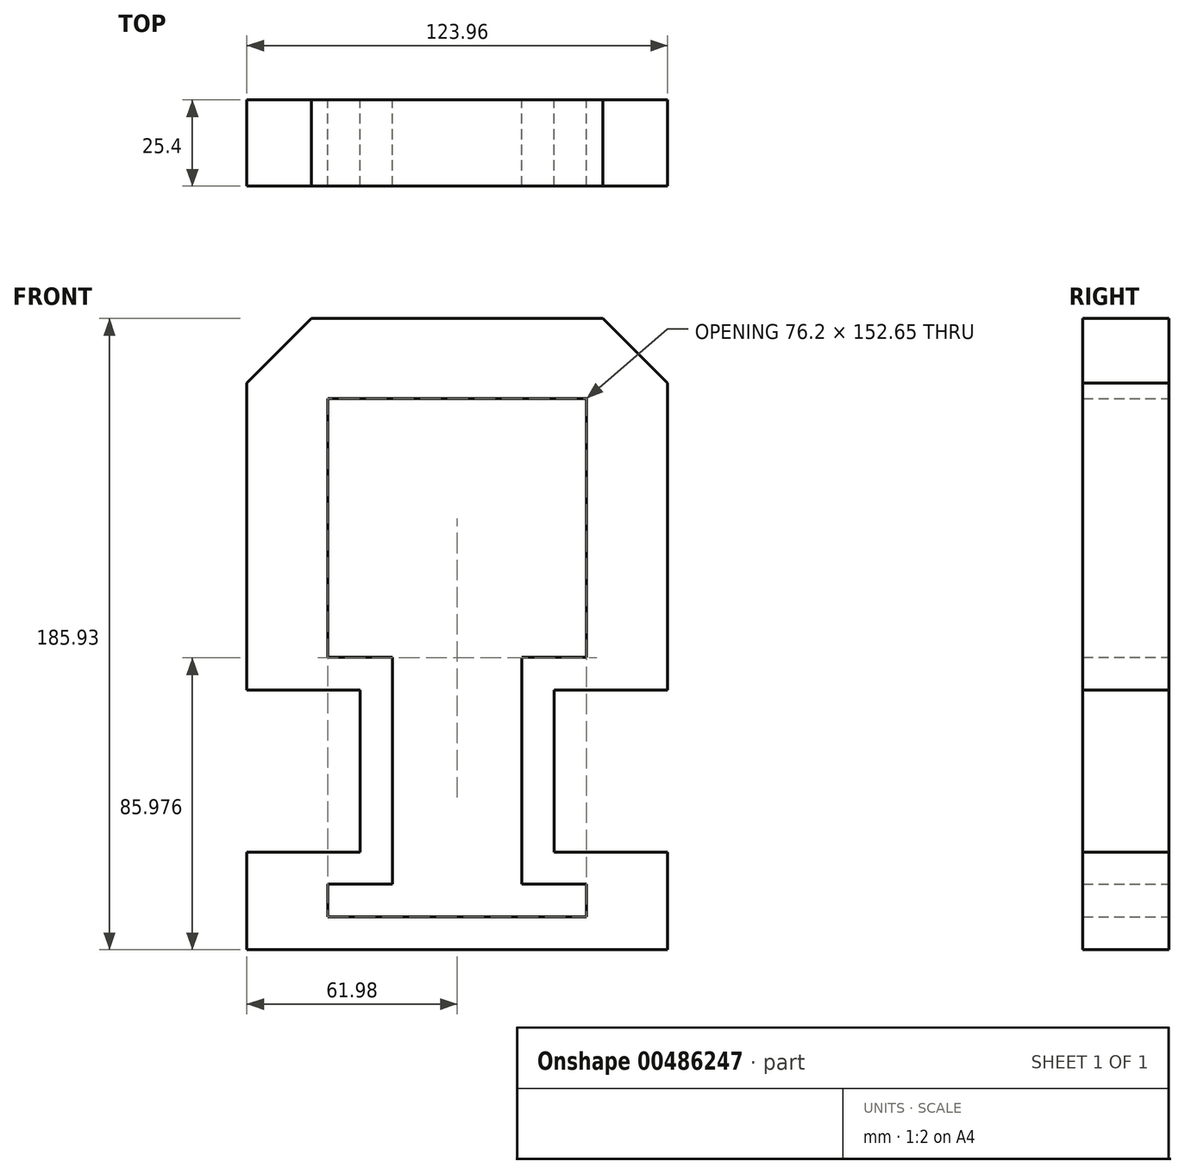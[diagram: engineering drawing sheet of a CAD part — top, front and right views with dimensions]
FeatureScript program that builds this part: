
annotation { "Feature Type Name" : "Feature", "Feature Type Description" : "" }
export const myFeature = defineFeature(function(context is Context, id is Id, definition is map)
    precondition{}
    {
        {
            var Q0;
            Q0=qCreatedBy(makeId("Front.planeOp"),FACE);
            var sketch = newSketch(context, id + "F0", { "sketchPlane" : qUnion([Q0])});
            skLineSegment(sketch, "E0", {"start": v(0, 54.64) * mm, "end": v(38.1, 54.64) * mm});
            skLineSegment(sketch, "E1", {"start": v(38.1, 54.64) * mm, "end": v(0, 54.64) * mm});
            skLineSegment(sketch, "E2", {"start": v(-38.1, 54.64) * mm, "end": v(0, 54.64) * mm});
            skLineSegment(sketch, "E3", {"start": v(-38.1, 54.64) * mm, "end": v(-38.1, -21.56) * mm});
            skLineSegment(sketch, "E4", {"start": v(-38.1, -21.56) * mm, "end": v(-38.1, 54.64) * mm});
            skLineSegment(sketch, "E5", {"start": v(38.1, 54.64) * mm, "end": v(38.1, -21.56) * mm});
            skLineSegment(sketch, "E6", {"start": v(38.1, -21.56) * mm, "end": v(38.1, 54.64) * mm});
            skLineSegment(sketch, "E7", {"start": v(-38.1, -21.56) * mm, "end": v(-19.05, -21.56) * mm});
            skLineSegment(sketch, "E8", {"start": v(-19.05, -21.56) * mm, "end": v(-38.1, -21.56) * mm});
            skLineSegment(sketch, "E9", {"start": v(38.1, -21.56) * mm, "end": v(19.05, -21.56) * mm});
            skLineSegment(sketch, "E10", {"start": v(19.05, -21.56) * mm, "end": v(38.1, -21.56) * mm});
            skLineSegment(sketch, "E11", {"start": v(-19.05, -21.56) * mm, "end": v(-19.05, -88.36) * mm});
            skLineSegment(sketch, "E12", {"start": v(-19.05, -88.36) * mm, "end": v(-19.05, -21.56) * mm});
            skLineSegment(sketch, "E13", {"start": v(19.05, -21.56) * mm, "end": v(19.05, -88.36) * mm});
            skLineSegment(sketch, "E14", {"start": v(19.05, -88.36) * mm, "end": v(19.05, -21.56) * mm});
            skLineSegment(sketch, "E15", {"start": v(19.05, -88.36) * mm, "end": v(38.1, -88.36) * mm});
            skLineSegment(sketch, "E16", {"start": v(38.1, -88.36) * mm, "end": v(19.05, -88.36) * mm});
            skLineSegment(sketch, "E17", {"start": v(-19.05, -88.36) * mm, "end": v(-38.1, -88.36) * mm});
            skLineSegment(sketch, "E18", {"start": v(-38.1, -88.36) * mm, "end": v(-19.05, -88.36) * mm});
            skLineSegment(sketch, "E19", {"start": v(-38.1, -88.36) * mm, "end": v(-38.1, -98.01) * mm});
            skLineSegment(sketch, "E20", {"start": v(-38.1, -98.01) * mm, "end": v(-38.1, -88.36) * mm});
            skLineSegment(sketch, "E21", {"start": v(-38.1, -98.01) * mm, "end": v(38.1, -98.01) * mm});
            skLineSegment(sketch, "E22", {"start": v(38.1, -98.01) * mm, "end": v(38.1, -88.36) * mm});
            skLineSegment(sketch, "E23", {"start": v(0, -107.66) * mm, "end": v(61.98, -107.66) * mm});
            skLineSegment(sketch, "E24", {"start": v(61.98, -107.66) * mm, "end": v(0, -107.66) * mm});
            skLineSegment(sketch, "E25", {"start": v(-61.98, -107.66) * mm, "end": v(0, -107.66) * mm});
            skLineSegment(sketch, "E26", {"start": v(61.98, -107.66) * mm, "end": v(61.98, -78.96) * mm});
            skLineSegment(sketch, "E27", {"start": v(61.98, -78.96) * mm, "end": v(61.98, -107.66) * mm});
            skLineSegment(sketch, "E28", {"start": v(-61.98, -107.66) * mm, "end": v(-61.98, -78.96) * mm});
            skLineSegment(sketch, "E29", {"start": v(-61.98, -78.96) * mm, "end": v(-28.57, -78.96) * mm});
            skLineSegment(sketch, "E30", {"start": v(-28.57, -78.96) * mm, "end": v(-61.98, -78.96) * mm});
            skLineSegment(sketch, "E31", {"start": v(61.98, -78.96) * mm, "end": v(28.58, -78.96) * mm});
            skLineSegment(sketch, "E32", {"start": v(28.58, -78.96) * mm, "end": v(61.98, -78.96) * mm});
            skLineSegment(sketch, "E33", {"start": v(-28.57, -78.96) * mm, "end": v(-28.57, -31.2) * mm});
            skLineSegment(sketch, "E34", {"start": v(28.58, -78.96) * mm, "end": v(28.58, -31.2) * mm});
            skLineSegment(sketch, "E35", {"start": v(28.58, -31.2) * mm, "end": v(61.98, -31.2) * mm});
            skLineSegment(sketch, "E36", {"start": v(61.98, -31.2) * mm, "end": v(28.58, -31.2) * mm});
            skLineSegment(sketch, "E37", {"start": v(-28.57, -31.2) * mm, "end": v(-61.98, -31.2) * mm});
            skLineSegment(sketch, "E38", {"start": v(-61.98, -31.2) * mm, "end": v(-61.98, 59.22) * mm});
            skLineSegment(sketch, "E39", {"start": v(61.98, -31.2) * mm, "end": v(61.98, 59.22) * mm});
            skLineSegment(sketch, "E40", {"start": v(0, 54.64) * mm, "end": v(0, 78.27) * mm});
            skLineSegment(sketch, "E41", {"start": v(0, 78.27) * mm, "end": v(-42.93, 78.27) * mm});
            skLineSegment(sketch, "E42", {"start": v(-42.93, 78.27) * mm, "end": v(0, 78.27) * mm});
            skLineSegment(sketch, "E43", {"start": v(42.93, 78.27) * mm, "end": v(0, 78.27) * mm});
            skLineSegment(sketch, "E44", {"start": v(-61.98, 59.22) * mm, "end": v(-42.93, 78.27) * mm});
            skLineSegment(sketch, "E45", {"start": v(61.98, 59.22) * mm, "end": v(42.93, 78.27) * mm});
            skSolve(sketch);
        }
        {
            var Q0;
            Q0 = qSketchRegion(id + "F0", true);
            extrude(context, id + "F1", {"entities" : qUnion([Q0]), "depth" : 25.4 * mm});
        }
    });
